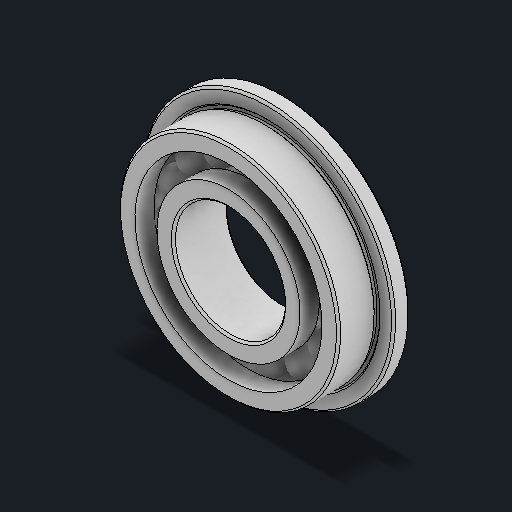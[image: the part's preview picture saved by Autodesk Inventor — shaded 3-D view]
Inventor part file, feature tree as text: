
AUTODESK INVENTOR PART (.ipt)
format: ipt  version: 2024 (Build 280153000, 153)  size: 697,856 bytes
history: native  units: in
note: dims shown in document units (in); Inventor stores cm internally (conversion verified against a paired STEP export)
features: other x14, fillet x2, revolve x1
ambient origin geometry x8: Origin, YZ Plane, XZ Plane, XY Plane, X Axis, Y Axis, Z Axis, Center Point
bodies: Solid1 (feature_tree), Solid2 (feature_tree), Solid3 (feature_tree), Solid4 (feature_tree), Solid5 (feature_tree), Solid6 (feature_tree), Solid7 (feature_tree), Solid8 (feature_tree), Solid9 (feature_tree), Solid10 (feature_tree), Solid11 (feature_tree), Solid12 (feature_tree), Solid13 (feature_tree), Solid14 (feature_tree), Solid15 (feature_tree), Solid16 (feature_tree), Solid17 (feature_tree)
feature tree (17):
  fillet  "Fillet1"  [1 undecoded]
  fillet  "Fillet2"  [1 undecoded]
  revolve  "Revolve3"  [1 undecoded]
  other  "CirPattern3[1]"
  other  "CirPattern3[2]"
  other  "CirPattern3[3]"
  other  "CirPattern3[4]"
  other  "CirPattern3[5]"
  other  "CirPattern3[6]"
  other  "CirPattern3[7]"
  other  "CirPattern3[8]"
  other  "CirPattern3[9]"
  other  "CirPattern3[10]"
  other  "CirPattern3[11]"
  other  "CirPattern3[12]"
  other  "CirPattern3[13]"
  other  "CirPattern3[14]"
note: 3 required parameter values undecoded (feature->parameter linkage not recoverable at this tier; creation-order binding heuristic only, values carry confidence <= 0.55)
